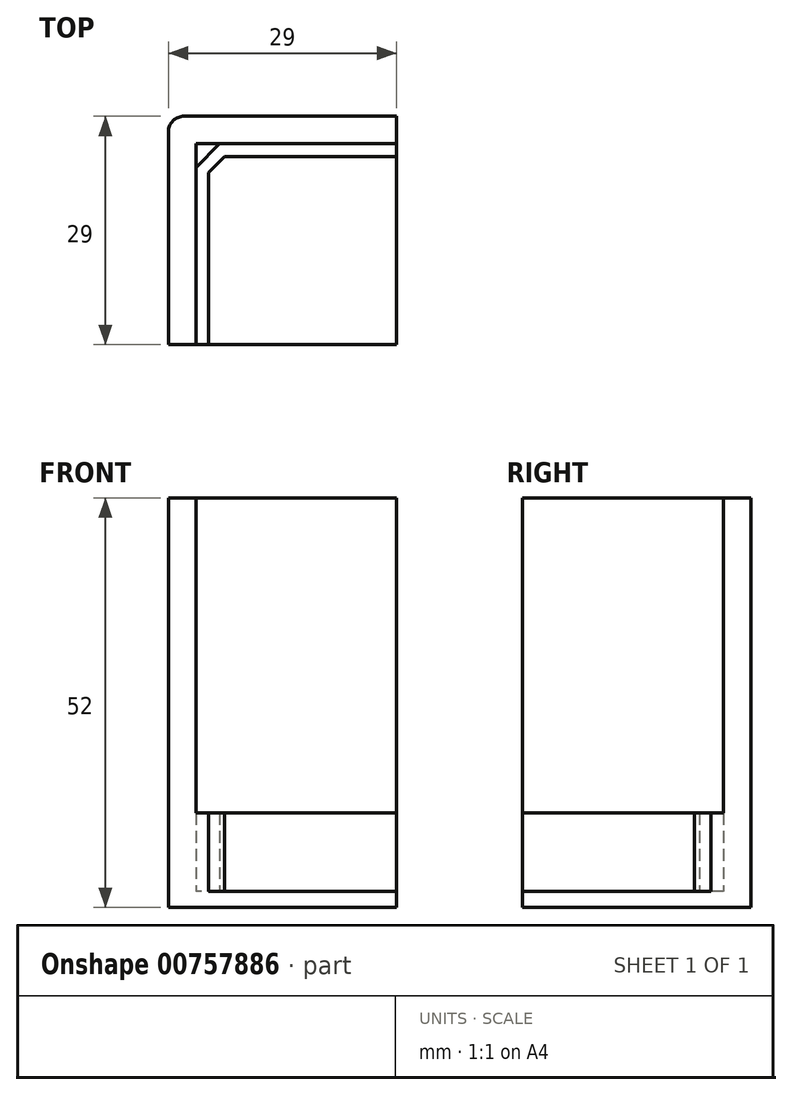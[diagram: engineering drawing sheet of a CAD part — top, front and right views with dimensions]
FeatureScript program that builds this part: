
annotation { "Feature Type Name" : "Feature", "Feature Type Description" : "" }
export const myFeature = defineFeature(function(context is Context, id is Id, definition is map)
    precondition{}
    {
        {
            var Q0;
            Q0=qCreatedBy(makeId("Top.planeOp"),FACE);
            var sketch = newSketch(context, id + "F0", { "sketchPlane" : qUnion([Q0])});
            skLineSegment(sketch, "E0", {"start": v(0, 0) * mm, "end": v(29, 0) * mm});
            skLineSegment(sketch, "E1", {"start": v(29, 0) * mm, "end": v(29, -3.5) * mm});
            skLineSegment(sketch, "E2", {"start": v(29, -3.5) * mm, "end": v(3.5, -3.5) * mm});
            skLineSegment(sketch, "E3", {"start": v(3.5, -3.5) * mm, "end": v(3.5, -29) * mm});
            skLineSegment(sketch, "E4", {"start": v(3.5, -29) * mm, "end": v(0, -29) * mm});
            skLineSegment(sketch, "E5", {"start": v(0, -29) * mm, "end": v(0, 0) * mm});
            skSolve(sketch);
        }
        {
            var Q0;
            Q0 = qSketchRegion(id + "F0", true);
            extrude(context, id + "F1", {"entities" : qUnion([Q0]), "depth" : 50 * mm, "offsetDistance" : 25 * mm});
        }
        {
            var Q0;
            Q0=qCreatedBy(makeId("Top.planeOp"),FACE);
            var sketch = newSketch(context, id + "F2", { "sketchPlane" : qUnion([Q0])});
            skLineSegment(sketch, "E6.bottom", {"start": v(0, 0) * mm, "end": v(29, 0) * mm});
            skLineSegment(sketch, "E6.top", {"start": v(0, -29) * mm, "end": v(29, -29) * mm});
            skLineSegment(sketch, "E6.left", {"start": v(0, 0) * mm, "end": v(0, -29) * mm});
            skLineSegment(sketch, "E6.right", {"start": v(29, 0) * mm, "end": v(29, -29) * mm});
            skSolve(sketch);
        }
        {
            var Q0;
            Q0 = qSketchRegion(id + "F2", true);
            extrude(context, id + "F3", {"entities" : qUnion([Q0]), "oppositeDirection" : true, "depth" : 2 * mm, "offsetDistance" : 25 * mm});
        }
        {
            var Q0;
            Q0=makeQuery(id+"F3.opExtrude","CAP_FACE",FACE,{"disambiguationData":[OSD([sQuery(id+"F2.wireOp",EDGE,"E6.bottom"),sQuery(id+"F2.wireOp",EDGE,"E6.top"),sQuery(id+"F2.wireOp",EDGE,"E6.left"),sQuery(id+"F2.wireOp",EDGE,"E6.right")])],"isStart":true});
            var sketch = newSketch(context, id + "F4", { "sketchPlane" : qUnion([Q0])});
            skLineSegment(sketch, "E7", {"start": v(5.1, -29) * mm, "end": v(5.1, -7.16) * mm});
            skLineSegment(sketch, "E8", {"start": v(5.1, -7.16) * mm, "end": v(7.16, -5.1) * mm});
            skLineSegment(sketch, "E9", {"start": v(7.16, -5.1) * mm, "end": v(29, -5.1) * mm});
            skLineSegment(sketch, "E10", {"start": v(5.1, -29) * mm, "end": v(3.5, -29) * mm});
            skLineSegment(sketch, "E11", {"start": v(3.5, -29) * mm, "end": v(3.5, -6.5) * mm});
            skLineSegment(sketch, "E12", {"start": v(3.5, -6.5) * mm, "end": v(6.5, -3.5) * mm});
            skLineSegment(sketch, "E13", {"start": v(6.5, -3.5) * mm, "end": v(29, -3.5) * mm});
            skLineSegment(sketch, "E14", {"start": v(29, -3.5) * mm, "end": v(29, -5.1) * mm});
            skSolve(sketch);
        }
        {
            var Q0;
            Q0 = qSketchRegion(id + "F4", true);
            extrude(context, id + "F5", {"entities" : qUnion([Q0]), "operationType" : NewBodyOperationType.ADD, "depth" : 10 * mm, "offsetDistance" : 25 * mm});
        }
        {
            var Q0;
            Q0=makeQuery(id+"F3.opExtrude","SWEPT_EDGE",EDGE,{"disambiguationData":[OSD([sQuery(id+"F2.wireOp",EDGE,"E6.bottom"),sQuery(id+"F2.wireOp",EDGE,"E6.left")])]});
            fillet(context, id + "F6", {"entities" : qUnion([Q0]), "radius" : 2 * mm, "tangentPropagation" : true, "allowEdgeOverflow" : false});
        }
    });
